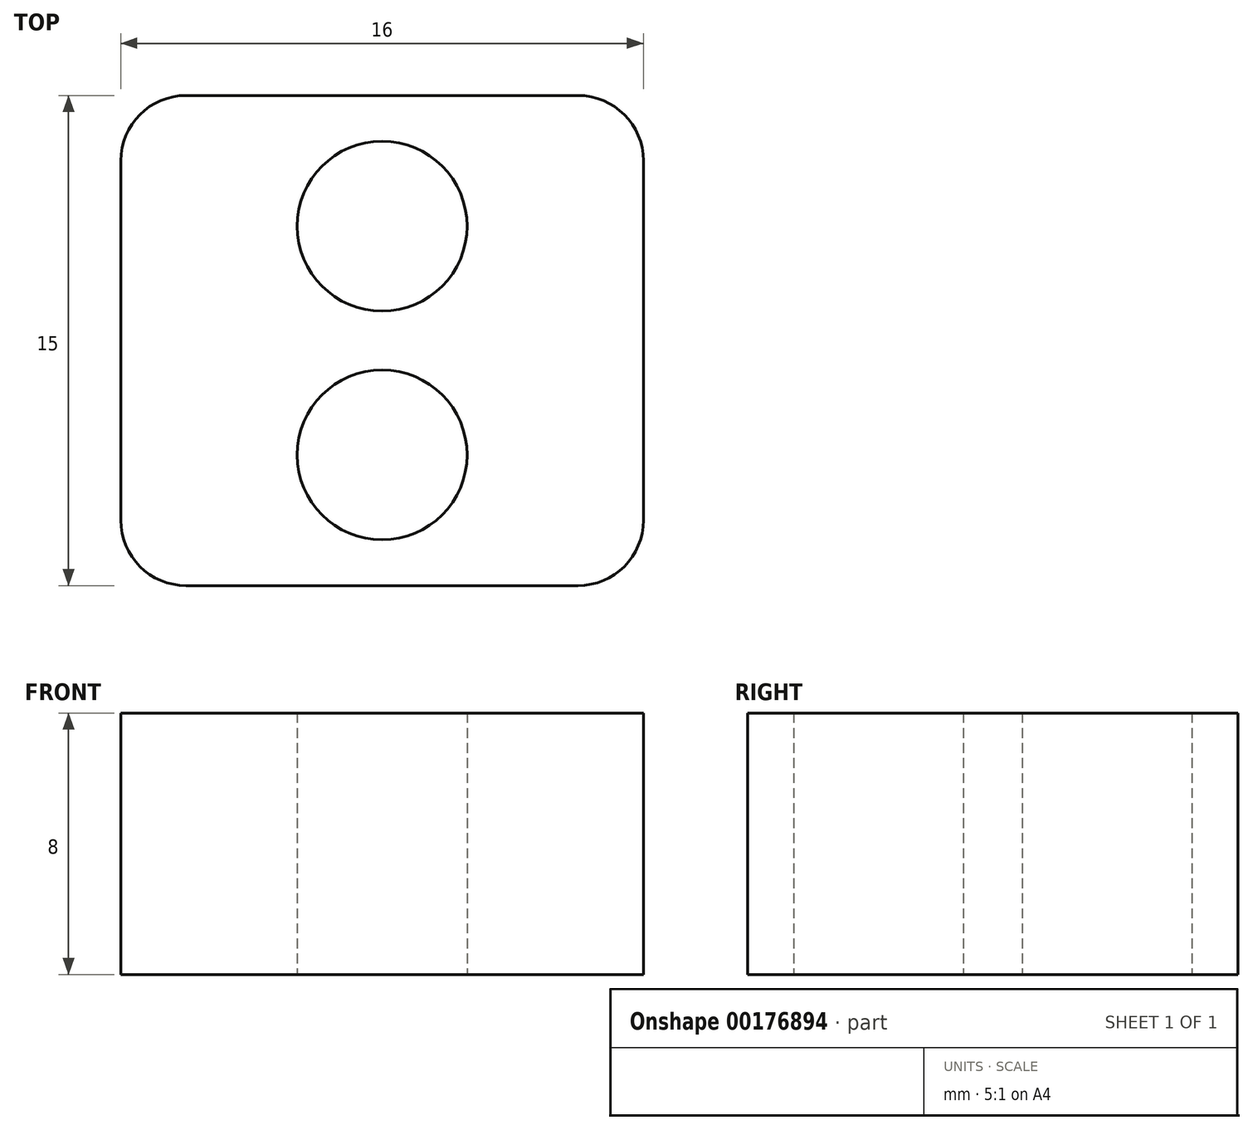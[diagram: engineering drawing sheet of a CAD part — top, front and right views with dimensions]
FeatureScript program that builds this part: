
annotation { "Feature Type Name" : "Feature", "Feature Type Description" : "" }
export const myFeature = defineFeature(function(context is Context, id is Id, definition is map)
    precondition{}
    {
        {
            var Q0;
            Q0=qCreatedBy(makeId("Top.planeOp"),FACE);
            var sketch = newSketch(context, id + "F0", { "sketchPlane" : qUnion([Q0])});
            skLineSegment(sketch, "E0.bottom", {"start": v(12.03, 22.72) * mm, "end": v(24.03, 22.72) * mm});
            skLineSegment(sketch, "E0.top", {"start": v(12.03, 7.72) * mm, "end": v(24.03, 7.72) * mm});
            skLineSegment(sketch, "E0.left", {"start": v(10.03, 20.72) * mm, "end": v(10.03, 9.72) * mm});
            skLineSegment(sketch, "E0.right", {"start": v(26.03, 20.72) * mm, "end": v(26.03, 9.72) * mm});
            skCircle(sketch, "E1", {"center": v(18.03, 18.72) * mm, "radius": 2.6 * mm});
            skCircle(sketch, "E2", {"center": v(18.03, 11.72) * mm, "radius": 2.6 * mm});
            skLineSegment(sketch, "E3", {"start": v(18.03, 18.72) * mm, "end": v(18.03, 11.72) * mm});
            skPoint(sketch, "E4.visualSharp", {"position": v(10.03, 22.72) * mm});
            skArc(sketch, "E4.filletArc", {"start": v(12.03, 22.72) * mm, "mid": v(10.62, 22.13) * mm, "end": v(10.03, 20.72) * mm});
            skPoint(sketch, "E5.visualSharp", {"position": v(26.03, 22.72) * mm});
            skArc(sketch, "E5.filletArc", {"start": v(26.03, 20.72) * mm, "mid": v(25.45, 22.13) * mm, "end": v(24.03, 22.72) * mm});
            skPoint(sketch, "E6.visualSharp", {"position": v(26.03, 7.72) * mm});
            skArc(sketch, "E6.filletArc", {"start": v(24.03, 7.72) * mm, "mid": v(25.45, 8.3) * mm, "end": v(26.03, 9.72) * mm});
            skPoint(sketch, "E7.visualSharp", {"position": v(10.03, 7.72) * mm});
            skArc(sketch, "E7.filletArc", {"start": v(10.03, 9.72) * mm, "mid": v(10.62, 8.3) * mm, "end": v(12.03, 7.72) * mm});
            skSolve(sketch);
        }
        {
            var Q0;
            Q0=makeQuery(id+"F0.imprint","IMPRINT",FACE,{"disambiguationData":[TD([[makeQuery(id+"F0.imprint","IMPRINT",EDGE,{"derivedFrom":sQuery(id+"F0.wireOp",EDGE,"E0.bottom")}),-1.0]])]});
            extrude(context, id + "F1", {"entities" : qUnion([Q0]), "depth" : 8 * mm});
        }
    });
